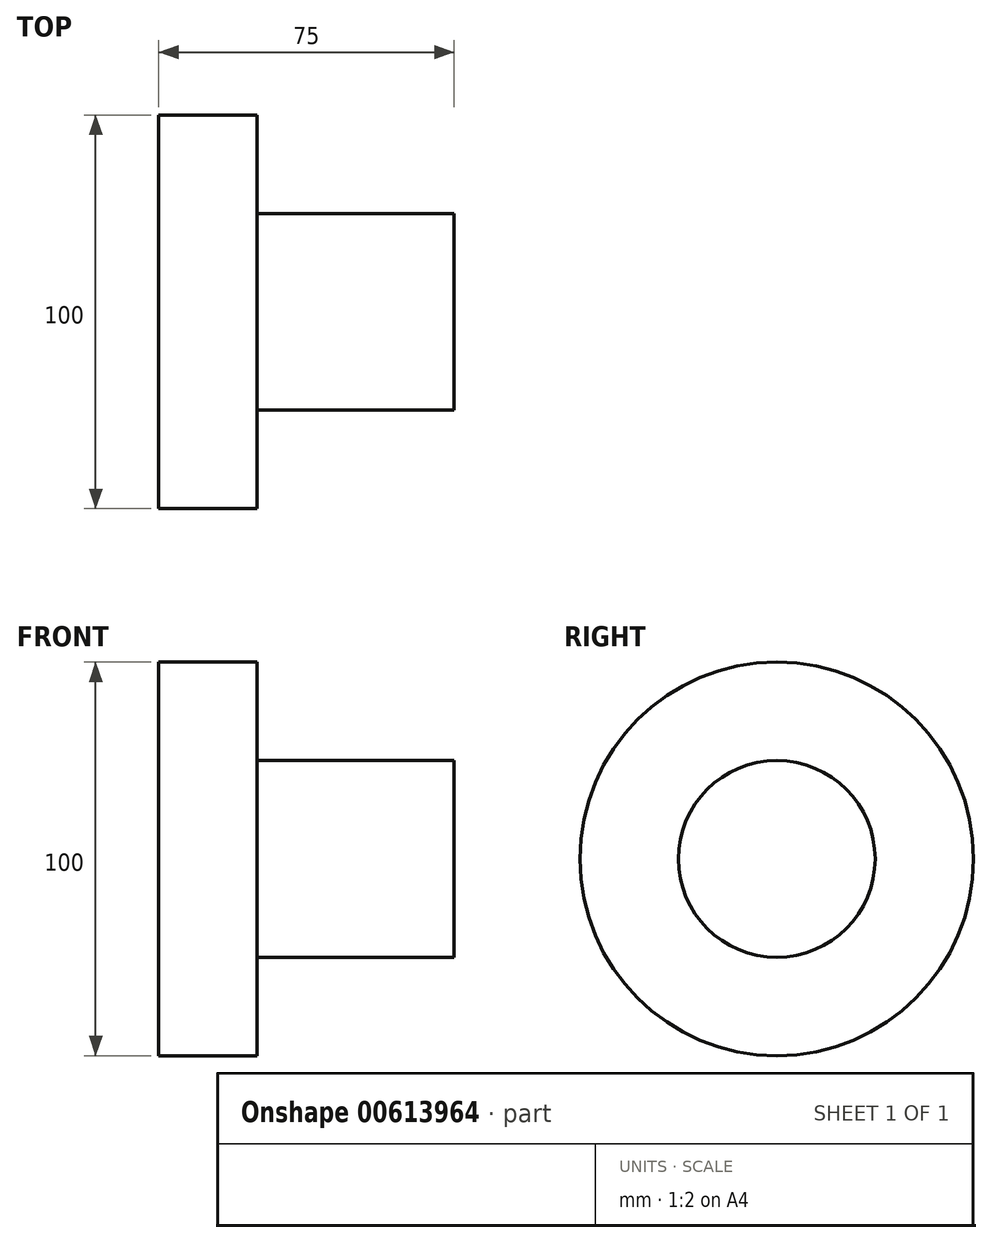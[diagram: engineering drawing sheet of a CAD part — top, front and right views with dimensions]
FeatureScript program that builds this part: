
annotation { "Feature Type Name" : "Feature", "Feature Type Description" : "" }
export const myFeature = defineFeature(function(context is Context, id is Id, definition is map)
    precondition{}
    {
        {
            var Q0;
            Q0=qCreatedBy(makeId("Front.planeOp"),FACE);
            var sketch = newSketch(context, id + "F0", { "sketchPlane" : qUnion([Q0])});
            skLineSegment(sketch, "E0", {"start": v(0, 0) * mm, "end": v(0, 50) * mm});
            skLineSegment(sketch, "E1", {"start": v(0, 50) * mm, "end": v(25, 50) * mm});
            skLineSegment(sketch, "E2", {"start": v(25, 50) * mm, "end": v(25, 0) * mm});
            skLineSegment(sketch, "E3", {"start": v(75, 0) * mm, "end": v(75, 25) * mm});
            skLineSegment(sketch, "E4", {"start": v(75, 25) * mm, "end": v(25, 25) * mm});
            skLineSegment(sketch, "E5", {"start": v(0, 0) * mm, "end": v(75, 0) * mm});
            skSolve(sketch);
        }
        {
            var Q0;
            Q0 = qSketchRegion(id + "F0", true);
            var Q1;
            Q1=sQuery(id+"F0.wireOp",EDGE,"E5");
            revolve(context, id + "F1", {"entities" : qUnion([Q0]), "axis" : qUnion([Q1]), "revolveType" : RevolveType.FULL});
        }
    });
